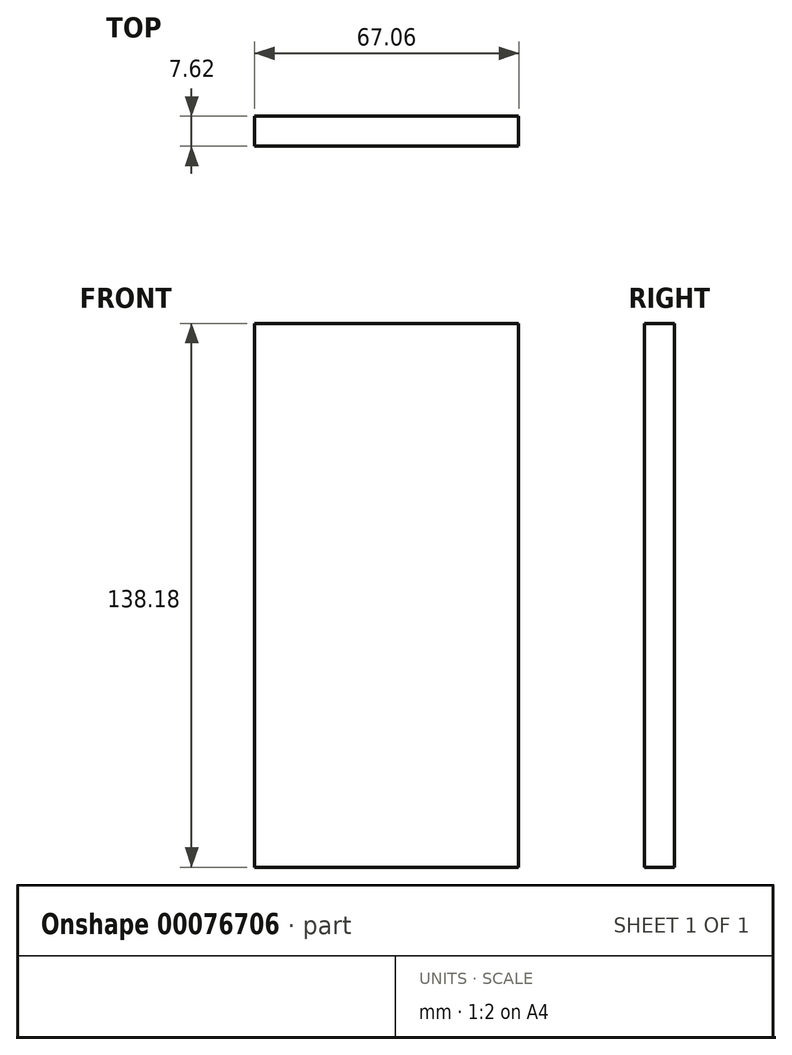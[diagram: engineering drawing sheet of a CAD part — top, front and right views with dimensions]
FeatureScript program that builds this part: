
annotation { "Feature Type Name" : "Feature", "Feature Type Description" : "" }
export const myFeature = defineFeature(function(context is Context, id is Id, definition is map)
    precondition{}
    {
        {
            var Q0;
            Q0=qCreatedBy(makeId("Front.planeOp"),FACE);
            var sketch = newSketch(context, id + "F0", { "sketchPlane" : qUnion([Q0])});
            skLineSegment(sketch, "E0.bottom", {"start": v(-33.53, 69.09) * mm, "end": v(33.53, 69.09) * mm});
            skLineSegment(sketch, "E0.top", {"start": v(-33.53, -69.09) * mm, "end": v(33.53, -69.09) * mm});
            skLineSegment(sketch, "E0.left", {"start": v(-33.53, 69.09) * mm, "end": v(-33.53, -69.09) * mm});
            skLineSegment(sketch, "E0.right", {"start": v(33.53, 69.09) * mm, "end": v(33.53, -69.09) * mm});
            skPoint(sketch, "E0.middle", {"position": v(0, 0) * mm});
            skSolve(sketch);
        }
        {
            var Q0;
            Q0=makeQuery(id+"F0.imprint","IMPRINT",FACE,{"disambiguationData":[TD([[makeQuery(id+"F0.imprint","IMPRINT",EDGE,{"derivedFrom":sQuery(id+"F0.wireOp",EDGE,"E0.bottom")}),-1.0]])]});
            extrude(context, id + "F1", {"entities" : qUnion([Q0]), "endBound" : BoundingType.SYMMETRIC, "depth" : 7.62 * mm});
        }
    });
